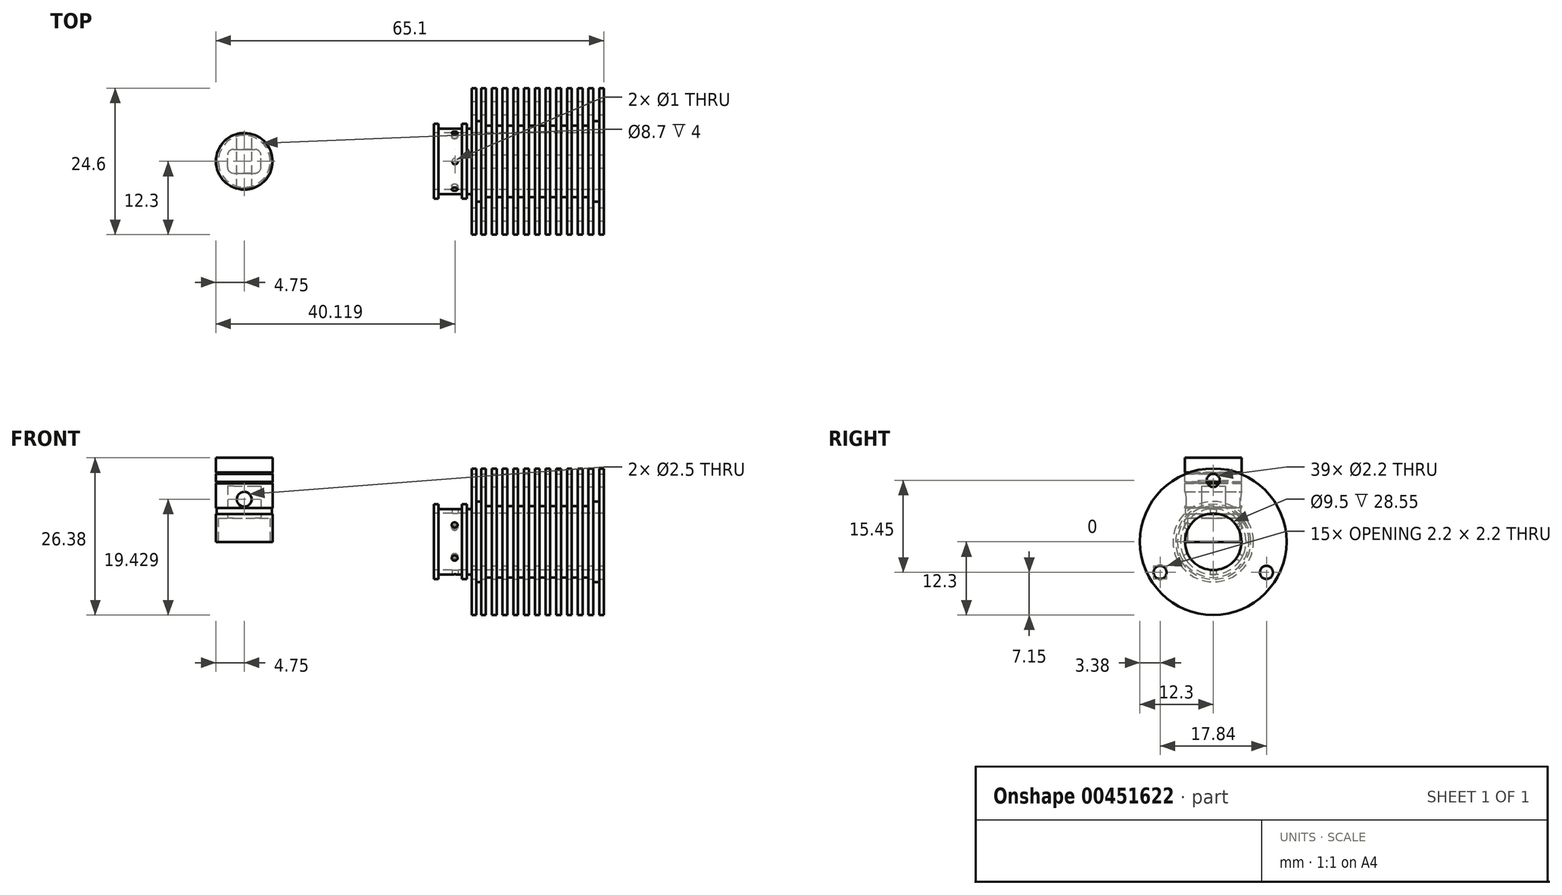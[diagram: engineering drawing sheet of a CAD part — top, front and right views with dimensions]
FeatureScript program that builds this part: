
annotation { "Feature Type Name" : "Feature", "Feature Type Description" : "" }
export const myFeature = defineFeature(function(context is Context, id is Id, definition is map)
    precondition{}
    {
        {
            var Q0;
            Q0=qCreatedBy(makeId("Front.planeOp"),FACE);
            var sketch = newSketch(context, id + "F0", { "sketchPlane" : qUnion([Q0])});
            skPoint(sketch, "E0.middle", {"position": v(0, 0) * mm});
            skLineSegment(sketch, "E1", {"start": v(0, -0.02) * mm, "end": v(0, 14.08) * mm});
            skLineSegment(sketch, "E2", {"start": v(-4.75, 14.08) * mm, "end": v(-4.75, 11.63) * mm});
            skLineSegment(sketch, "E3", {"start": v(-4.75, 4.68) * mm, "end": v(-4.62, 4.68) * mm});
            skLineSegment(sketch, "E4", {"start": v(-4.62, 4.68) * mm, "end": v(-4.62, 5.68) * mm});
            skLineSegment(sketch, "E5", {"start": v(-4.62, 5.68) * mm, "end": v(-4.75, 5.68) * mm});
            skLineSegment(sketch, "E6", {"start": v(-4.75, 10.03) * mm, "end": v(-4.62, 9.9) * mm});
            skLineSegment(sketch, "E7", {"start": v(-4.62, 9.9) * mm, "end": v(-4.75, 9.77) * mm});
            skLineSegment(sketch, "E8", {"start": v(-4.75, 11.63) * mm, "end": v(-4.62, 11.5) * mm});
            skLineSegment(sketch, "E9", {"start": v(-4.62, 11.5) * mm, "end": v(-4.75, 11.37) * mm});
            skLineSegment(sketch, "E10.trimOffspring", {"start": v(-4.75, 11.37) * mm, "end": v(-4.75, 10.03) * mm});
            skLineSegment(sketch, "E11.trimOffspring", {"start": v(-4.75, 9.77) * mm, "end": v(-4.75, 5.68) * mm});
            skLineSegment(sketch, "E12.trimOffspring", {"start": v(-4.75, 4.68) * mm, "end": v(-4.75, -0.02) * mm});
            skLineSegment(sketch, "E13", {"start": v(-4.75, 14.08) * mm, "end": v(0, 14.08) * mm});
            skLineSegment(sketch, "E14", {"start": v(-4.75, -0.02) * mm, "end": v(0, -0.02) * mm});
            skLineSegment(sketch, "E15", {"start": v(0, 14.08) * mm, "end": v(0, -6.41) * mm, "construction": true});
            skSolve(sketch);
        }
        {
            var Q0;
            {var subQ0=sQuery(id+"F0.wireOp",EDGE,"eGdi0r23-MWlI-d9Id-6IcZ-tQ7A4gUvsILz.left");Q0=makeQuery(id+"F0.imprint","IMPRINT",FACE,{"disambiguationData":[TD([[makeQuery(id+"F0.imprint","IMPRINT",EDGE,{"derivedFrom":subQ0}),1.0]])]});}
            var Q1;
            Q1=makeQuery(id+"F0.imprint","IMPRINT",FACE,{"disambiguationData":[TD([[makeQuery(id+"F0.imprint","IMPRINT",EDGE,{"derivedFrom":sQuery(id+"F0.wireOp",EDGE,"E1")}),1.0]])]});
            var Q2;
            Q2=sQuery(id+"F0.wireOp",EDGE,"E15");
            revolve(context, id + "F1", {"entities" : qUnion([Q0, Q1]), "axis" : qUnion([Q2]), "revolveType" : RevolveType.FULL});
        }
        {
            var Q0;
            Q0=qCreatedBy(makeId("Front.planeOp"),FACE);
            var sketch = newSketch(context, id + "F2", { "sketchPlane" : qUnion([Q0])});
            skPoint(sketch, "E16", {"position": v(0, 7.13) * mm});
            skCircle(sketch, "E17", {"center": v(0, 7.13) * mm, "radius": 1.25 * mm});
            skSolve(sketch);
        }
        {
            var Q0;
            Q0=makeQuery(id+"F2.imprint","IMPRINT",FACE,{"disambiguationData":[TD([[makeQuery(id+"F2.imprint","IMPRINT",EDGE,{"derivedFrom":sQuery(id+"F2.wireOp",EDGE,"E17")}),1.0]])]});
            extrude(context, id + "F3", {"entities" : qUnion([Q0]), "operationType" : NewBodyOperationType.REMOVE, "endBound" : BoundingType.SYMMETRIC, "depth" : 10 * mm});
        }
        {
            var Q0;
            Q0=makeQuery(id+"F1.opRevolve","SWEPT_FACE",FACE,{"disambiguationData":[OSD([sQuery(id+"F0.wireOp",EDGE,"E14")])]});
            var sketch = newSketch(context, id + "F4", { "sketchPlane" : qUnion([Q0])});
            skLineSegment(sketch, "E18.bottom", {"start": v(-1.8, 2) * mm, "end": v(1.8, 2) * mm});
            skLineSegment(sketch, "E18.top", {"start": v(-1.8, -2) * mm, "end": v(1.8, -2) * mm});
            skLineSegment(sketch, "E18.left", {"start": v(-2.8, 1) * mm, "end": v(-2.8, -1) * mm});
            skLineSegment(sketch, "E18.right", {"start": v(2.8, 1) * mm, "end": v(2.8, -1) * mm});
            skPoint(sketch, "E18.middle", {"position": v(0, 0) * mm});
            skCircle(sketch, "E19", {"center": v(0, 0) * mm, "radius": 4.35 * mm});
            skPoint(sketch, "E20.visualSharp", {"position": v(-2.8, 2) * mm});
            skArc(sketch, "E20.filletArc", {"start": v(-1.8, 2) * mm, "mid": v(-2.5, 1.7) * mm, "end": v(-2.8, 1) * mm});
            skPoint(sketch, "E21.visualSharp", {"position": v(-2.8, -2) * mm});
            skArc(sketch, "E21.filletArc", {"start": v(-2.8, -1) * mm, "mid": v(-2.5, -1.7) * mm, "end": v(-1.8, -2) * mm});
            skPoint(sketch, "E22.visualSharp", {"position": v(2.8, 2) * mm});
            skArc(sketch, "E22.filletArc", {"start": v(2.8, 1) * mm, "mid": v(2.5, 1.7) * mm, "end": v(1.8, 2) * mm});
            skPoint(sketch, "E23.visualSharp", {"position": v(2.8, -2) * mm});
            skArc(sketch, "E23.filletArc", {"start": v(1.8, -2) * mm, "mid": v(2.5, -1.7) * mm, "end": v(2.8, -1) * mm});
            skSolve(sketch);
        }
        {
            var Q0;
            Q0=makeQuery(id+"F4.imprint","IMPRINT",FACE,{"disambiguationData":[TD([[makeQuery(id+"F4.imprint","IMPRINT",EDGE,{"derivedFrom":sQuery(id+"F4.wireOp",EDGE,"E18.bottom")}),1.0]])]});
            var Q1;
            Q1=sQuery(id+"FsbAGgwMZmhRhTR_1.wireOp",EDGE,"XXkkC4YT-YGF8-Mw8t-M4hJ-ITye5uaQiXAc");
            extrude(context, id + "F5", {"entities" : qUnion([Q0]), "operationType" : NewBodyOperationType.REMOVE, "surfaceEntities" : qUnion([Q1]), "oppositeDirection" : true, "depth" : 4 * mm});
        }
        {
            var Q0;
            Q0=makeQuery(id+"F5.boolean.opBoolean","SPLIT",FACE,{"disambiguationData":[TD([makeQuery(id+"F5.opExtrude","SWEPT_FACE",FACE,{"disambiguationData":[OSD([sQuery(id+"F4.wireOp",EDGE,"E18.bottom")])]})])],"derivedFrom":makeQuery(id+"F1.opRevolve","SWEPT_FACE",FACE,{"disambiguationData":[OSD([sQuery(id+"F0.wireOp",EDGE,"E14")])]})});
            extrude(context, id + "F6", {"entities" : qUnion([Q0]), "operationType" : NewBodyOperationType.REMOVE, "oppositeDirection" : true, "depth" : 9.4 * mm});
        }
        {
            var Q0;
            Q0=qCreatedBy(makeId("Front.planeOp"),FACE);
            var sketch = newSketch(context, id + "F7", { "sketchPlane" : qUnion([Q0])});
            skPoint(sketch, "E24.0", {"position": v(0, 7.13) * mm});
            skCircle(sketch, "E24.1", {"center": v(0, 7.13) * mm, "radius": 1.25 * mm});
            skSolve(sketch);
        }
        {
            var Q0;
            Q0=makeQuery(id+"F7.imprint","IMPRINT",FACE,{"disambiguationData":[TD([[makeQuery(id+"F7.imprint","IMPRINT",EDGE,{"derivedFrom":sQuery(id+"F7.wireOp",EDGE,"E24.1")}),1.0]])]});
            extrude(context, id + "F8", {"entities" : qUnion([Q0]), "endBound" : BoundingType.SYMMETRIC, "depth" : 9 * mm});
        }
        {
            var Q0;
            Q0=qCreatedBy(makeId("Front.planeOp"),FACE);
            var sketch = newSketch(context, id + "F9", { "sketchPlane" : qUnion([Q0])});
            skLineSegment(sketch, "E25", {"start": v(27.89, 0) * mm, "end": v(63.64, 0) * mm, "construction": true});
            skLineSegment(sketch, "E26", {"start": v(31.8, 4.75) * mm, "end": v(60.35, 4.75) * mm});
            skLineSegment(sketch, "E27", {"start": v(60.35, 4.75) * mm, "end": v(60.35, 12.3) * mm});
            skLineSegment(sketch, "E28", {"start": v(59.55, 12.3) * mm, "end": v(59.55, 6.75) * mm});
            skLineSegment(sketch, "E29", {"start": v(59.55, 6.75) * mm, "end": v(58.55, 6.75) * mm});
            skLineSegment(sketch, "E30", {"start": v(60.35, 12.3) * mm, "end": v(59.55, 12.3) * mm});
            skLineSegment(sketch, "E31", {"start": v(40.24, 12.3) * mm, "end": v(39.75, 12.3) * mm});
            skLineSegment(sketch, "E32", {"start": v(39.75, 12.3) * mm, "end": v(39.75, 6.75) * mm});
            skLineSegment(sketch, "E33", {"start": v(38.95, 12.3) * mm, "end": v(38.15, 12.3) * mm});
            skLineSegment(sketch, "E34", {"start": v(38.15, 12.3) * mm, "end": v(38.15, 5.8) * mm});
            skLineSegment(sketch, "E35", {"start": v(38.95, 12.3) * mm, "end": v(38.95, 6.75) * mm});
            skLineSegment(sketch, "E36", {"start": v(38.95, 6.75) * mm, "end": v(39.75, 6.75) * mm});
            skLineSegment(sketch, "E37", {"start": v(31.8, 4.75) * mm, "end": v(31.8, 6.3) * mm});
            skLineSegment(sketch, "E38", {"start": v(31.8, 6.3) * mm, "end": v(32.6, 6.3) * mm});
            skLineSegment(sketch, "E39", {"start": v(32.6, 6.3) * mm, "end": v(32.6, 5.8) * mm});
            skLineSegment(sketch, "E40", {"start": v(32.9, 5.5) * mm, "end": v(36.25, 5.5) * mm});
            skLineSegment(sketch, "E41", {"start": v(36.55, 5.8) * mm, "end": v(36.55, 6.3) * mm});
            skLineSegment(sketch, "E42", {"start": v(36.55, 6.3) * mm, "end": v(37.35, 6.3) * mm});
            skLineSegment(sketch, "E43", {"start": v(37.35, 6.3) * mm, "end": v(37.35, 5.8) * mm});
            skLineSegment(sketch, "E44", {"start": v(37.65, 5.5) * mm, "end": v(37.85, 5.5) * mm});
            skLineSegment(sketch, "E45", {"start": v(58.55, 6.75) * mm, "end": v(58.55, 12.3) * mm});
            skLineSegment(sketch, "E46", {"start": v(58.55, 12.3) * mm, "end": v(57.75, 12.3) * mm});
            skLineSegment(sketch, "E47", {"start": v(57.75, 12.3) * mm, "end": v(57.75, 6) * mm});
            skLineSegment(sketch, "E48", {"start": v(57.75, 6) * mm, "end": v(56.75, 6) * mm});
            skLineSegment(sketch, "E49", {"start": v(56.75, 6) * mm, "end": v(56.75, 12.3) * mm});
            skLineSegment(sketch, "E50", {"start": v(56.75, 12.3) * mm, "end": v(55.95, 12.3) * mm});
            skLineSegment(sketch, "E51", {"start": v(55.95, 12.3) * mm, "end": v(55.95, 6) * mm});
            skLineSegment(sketch, "E52.1.0.0", {"start": v(55.95, 6) * mm, "end": v(54.95, 6) * mm});
            skLineSegment(sketch, "E52.1.0.1", {"start": v(54.95, 6) * mm, "end": v(54.95, 12.3) * mm});
            skLineSegment(sketch, "E52.1.0.2", {"start": v(54.95, 12.3) * mm, "end": v(54.15, 12.3) * mm});
            skLineSegment(sketch, "E52.1.0.3", {"start": v(54.15, 12.3) * mm, "end": v(54.15, 6) * mm});
            skLineSegment(sketch, "E52.2.0.0", {"start": v(54.15, 6) * mm, "end": v(53.15, 6) * mm});
            skLineSegment(sketch, "E52.2.0.1", {"start": v(53.15, 6) * mm, "end": v(53.15, 12.3) * mm});
            skLineSegment(sketch, "E52.2.0.2", {"start": v(53.15, 12.3) * mm, "end": v(52.35, 12.3) * mm});
            skLineSegment(sketch, "E52.2.0.3", {"start": v(52.35, 12.3) * mm, "end": v(52.35, 6) * mm});
            skLineSegment(sketch, "E52.3.0.0", {"start": v(52.35, 6) * mm, "end": v(51.35, 6) * mm});
            skLineSegment(sketch, "E52.3.0.1", {"start": v(51.35, 6) * mm, "end": v(51.35, 12.3) * mm});
            skLineSegment(sketch, "E52.3.0.2", {"start": v(51.35, 12.3) * mm, "end": v(50.55, 12.3) * mm});
            skLineSegment(sketch, "E52.3.0.3", {"start": v(50.55, 12.3) * mm, "end": v(50.55, 6) * mm});
            skLineSegment(sketch, "E52.4.0.0", {"start": v(50.55, 6) * mm, "end": v(49.55, 6) * mm});
            skLineSegment(sketch, "E52.4.0.1", {"start": v(49.55, 6) * mm, "end": v(49.55, 12.3) * mm});
            skLineSegment(sketch, "E52.4.0.2", {"start": v(49.55, 12.3) * mm, "end": v(48.75, 12.3) * mm});
            skLineSegment(sketch, "E52.4.0.3", {"start": v(48.75, 12.3) * mm, "end": v(48.75, 6) * mm});
            skLineSegment(sketch, "E52.5.0.0", {"start": v(48.75, 6) * mm, "end": v(47.75, 6) * mm});
            skLineSegment(sketch, "E52.5.0.1", {"start": v(47.75, 6) * mm, "end": v(47.75, 12.3) * mm});
            skLineSegment(sketch, "E52.5.0.2", {"start": v(47.75, 12.3) * mm, "end": v(46.95, 12.3) * mm});
            skLineSegment(sketch, "E52.5.0.3", {"start": v(46.95, 12.3) * mm, "end": v(46.95, 6) * mm});
            skLineSegment(sketch, "E52.6.0.0", {"start": v(46.95, 6) * mm, "end": v(45.95, 6) * mm});
            skLineSegment(sketch, "E52.6.0.1", {"start": v(45.95, 6) * mm, "end": v(45.95, 12.3) * mm});
            skLineSegment(sketch, "E52.6.0.2", {"start": v(45.95, 12.3) * mm, "end": v(45.15, 12.3) * mm});
            skLineSegment(sketch, "E52.6.0.3", {"start": v(45.15, 12.3) * mm, "end": v(45.15, 6) * mm});
            skLineSegment(sketch, "E52.7.0.0", {"start": v(45.15, 6) * mm, "end": v(44.15, 6) * mm});
            skLineSegment(sketch, "E52.7.0.1", {"start": v(44.15, 6) * mm, "end": v(44.15, 12.3) * mm});
            skLineSegment(sketch, "E52.7.0.2", {"start": v(44.15, 12.3) * mm, "end": v(43.35, 12.3) * mm});
            skLineSegment(sketch, "E52.7.0.3", {"start": v(43.35, 12.3) * mm, "end": v(43.35, 6) * mm});
            skLineSegment(sketch, "E52.8.0.0", {"start": v(43.35, 6) * mm, "end": v(42.35, 6) * mm});
            skLineSegment(sketch, "E52.8.0.1", {"start": v(42.35, 6) * mm, "end": v(42.35, 12.3) * mm});
            skLineSegment(sketch, "E52.8.0.2", {"start": v(42.35, 12.3) * mm, "end": v(41.55, 12.3) * mm});
            skLineSegment(sketch, "E52.8.0.3", {"start": v(41.55, 12.3) * mm, "end": v(41.55, 6) * mm});
            skLineSegment(sketch, "E52.9.0.0", {"start": v(41.55, 6) * mm, "end": v(40.55, 6) * mm});
            skLineSegment(sketch, "E52.9.0.1", {"start": v(40.55, 6) * mm, "end": v(40.55, 12.3) * mm});
            skLineSegment(sketch, "E52.9.0.2", {"start": v(40.55, 12.3) * mm, "end": v(39.75, 12.3) * mm});
            skLineSegment(sketch, "E52.9.0.3", {"start": v(39.75, 12.3) * mm, "end": v(39.75, 6) * mm});
            skLineSegment(sketch, "E52.direction1", {"start": v(56.75, 6) * mm, "end": v(54.95, 6) * mm, "construction": true});
            skPoint(sketch, "E53.visualSharp", {"position": v(37.35, 5.5) * mm});
            skArc(sketch, "E53.filletArc", {"start": v(37.35, 5.8) * mm, "mid": v(37.44, 5.59) * mm, "end": v(37.65, 5.5) * mm});
            skPoint(sketch, "E54.visualSharp", {"position": v(32.6, 5.5) * mm});
            skArc(sketch, "E54.filletArc", {"start": v(32.6, 5.8) * mm, "mid": v(32.69, 5.59) * mm, "end": v(32.9, 5.5) * mm});
            skPoint(sketch, "E55.visualSharp", {"position": v(38.15, 5.5) * mm});
            skArc(sketch, "E55.filletArc", {"start": v(37.85, 5.5) * mm, "mid": v(38.06, 5.59) * mm, "end": v(38.15, 5.8) * mm});
            skPoint(sketch, "E56.visualSharp", {"position": v(36.55, 5.5) * mm});
            skArc(sketch, "E56.filletArc", {"start": v(36.25, 5.5) * mm, "mid": v(36.46, 5.59) * mm, "end": v(36.55, 5.8) * mm});
            skPoint(sketch, "E57", {"position": v(35.3, 5.5) * mm});
            skSolve(sketch);
        }
        {
            var Q0;
            {var subQ0=sQuery(id+"F9.wireOp",EDGE,"E27");Q0=makeQuery(id+"F9.imprint","IMPRINT",FACE,{"disambiguationData":[TD([[makeQuery(id+"F9.imprint","IMPRINT",EDGE,{"derivedFrom":subQ0}),1.0]])]});}
            var Q1;
            Q1=sQuery(id+"F9.wireOp",EDGE,"E25");
            revolve(context, id + "F10", {"entities" : qUnion([Q0]), "axis" : qUnion([Q1]), "revolveType" : RevolveType.FULL});
        }
        {
            var Q0;
            Q0=makeQuery(id+"F10.opRevolve","SWEPT_FACE",FACE,{"disambiguationData":[OSD([sQuery(id+"F9.wireOp",EDGE,"E27")])]});
            var sketch = newSketch(context, id + "F11", { "sketchPlane" : qUnion([Q0])});
            skCircle(sketch, "E58", {"center": v(0, 0) * mm, "radius": 10.3 * mm, "construction": true});
            skPoint(sketch, "E59", {"position": v(0, 10.3) * mm});
            skPoint(sketch, "E60.1.1", {"position": v(-8.92, -5.15) * mm});
            skPoint(sketch, "E60.2.1", {"position": v(8.92, -5.15) * mm});
            skSolve(sketch);
        }
        {
            var Q0;
            Q0=sQuery(id+"F11.wireOp",VERTEX,"E59");
            var Q1;
            Q1=sQuery(id+"F11.wireOp",VERTEX,"E60.1.1");
            var Q2;
            Q2=sQuery(id+"F11.wireOp",VERTEX,"E60.2.1");
            var Q3;
            Q3=makeQuery(id+"F10.opRevolve","SWEPT_BODY",BODY,{"disambiguationData":[OSD([sQuery(id+"F9.wireOp",EDGE,"E26"),sQuery(id+"F9.wireOp",EDGE,"E27"),sQuery(id+"F9.wireOp",EDGE,"E28"),sQuery(id+"F9.wireOp",EDGE,"E29"),sQuery(id+"F9.wireOp",EDGE,"E30"),sQuery(id+"F9.wireOp",EDGE,"E33"),sQuery(id+"F9.wireOp",EDGE,"E34"),sQuery(id+"F9.wireOp",EDGE,"E35"),sQuery(id+"F9.wireOp",EDGE,"E36"),sQuery(id+"F9.wireOp",EDGE,"E37"),sQuery(id+"F9.wireOp",EDGE,"E38"),sQuery(id+"F9.wireOp",EDGE,"E39"),sQuery(id+"F9.wireOp",EDGE,"E40"),sQuery(id+"F9.wireOp",EDGE,"E41"),sQuery(id+"F9.wireOp",EDGE,"E42"),sQuery(id+"F9.wireOp",EDGE,"E43"),sQuery(id+"F9.wireOp",EDGE,"E44"),sQuery(id+"F9.wireOp",EDGE,"E45"),sQuery(id+"F9.wireOp",EDGE,"E46"),sQuery(id+"F9.wireOp",EDGE,"E47"),sQuery(id+"F9.wireOp",EDGE,"E48"),sQuery(id+"F9.wireOp",EDGE,"E49"),sQuery(id+"F9.wireOp",EDGE,"E50"),sQuery(id+"F9.wireOp",EDGE,"E51"),sQuery(id+"F9.wireOp",EDGE,"E52.1.0.0"),sQuery(id+"F9.wireOp",EDGE,"E52.1.0.1"),sQuery(id+"F9.wireOp",EDGE,"E52.1.0.2"),sQuery(id+"F9.wireOp",EDGE,"E52.1.0.3"),sQuery(id+"F9.wireOp",EDGE,"E52.2.0.0"),sQuery(id+"F9.wireOp",EDGE,"E52.2.0.1"),sQuery(id+"F9.wireOp",EDGE,"E52.2.0.2"),sQuery(id+"F9.wireOp",EDGE,"E52.2.0.3"),sQuery(id+"F9.wireOp",EDGE,"E52.3.0.0"),sQuery(id+"F9.wireOp",EDGE,"E52.3.0.1"),sQuery(id+"F9.wireOp",EDGE,"E52.3.0.2"),sQuery(id+"F9.wireOp",EDGE,"E52.3.0.3"),sQuery(id+"F9.wireOp",EDGE,"E52.4.0.0"),sQuery(id+"F9.wireOp",EDGE,"E52.4.0.1"),sQuery(id+"F9.wireOp",EDGE,"E52.4.0.2"),sQuery(id+"F9.wireOp",EDGE,"E52.4.0.3"),sQuery(id+"F9.wireOp",EDGE,"E52.5.0.0"),sQuery(id+"F9.wireOp",EDGE,"E52.5.0.1"),sQuery(id+"F9.wireOp",EDGE,"E52.5.0.2"),sQuery(id+"F9.wireOp",EDGE,"E52.5.0.3"),sQuery(id+"F9.wireOp",EDGE,"E52.6.0.0"),sQuery(id+"F9.wireOp",EDGE,"E52.6.0.1"),sQuery(id+"F9.wireOp",EDGE,"E52.6.0.2"),sQuery(id+"F9.wireOp",EDGE,"E52.6.0.3"),sQuery(id+"F9.wireOp",EDGE,"E52.7.0.0"),sQuery(id+"F9.wireOp",EDGE,"E52.7.0.1"),sQuery(id+"F9.wireOp",EDGE,"E52.7.0.2"),sQuery(id+"F9.wireOp",EDGE,"E52.7.0.3"),sQuery(id+"F9.wireOp",EDGE,"E52.8.0.0"),sQuery(id+"F9.wireOp",EDGE,"E52.8.0.1"),sQuery(id+"F9.wireOp",EDGE,"E52.8.0.2"),sQuery(id+"F9.wireOp",EDGE,"E52.8.0.3"),sQuery(id+"F9.wireOp",EDGE,"E52.9.0.0"),sQuery(id+"F9.wireOp",EDGE,"E52.9.0.1"),sQuery(id+"F9.wireOp",EDGE,"E52.9.0.2"),sQuery(id+"F9.wireOp",EDGE,"E52.9.0.3"),sQuery(id+"F9.wireOp",EDGE,"E53.filletArc"),sQuery(id+"F9.wireOp",EDGE,"E54.filletArc"),sQuery(id+"F9.wireOp",EDGE,"E55.filletArc"),sQuery(id+"F9.wireOp",EDGE,"E56.filletArc")])]});
            hole(context, id + "F12", {"style" : HoleStyle.SIMPLE, "endStyle" : HoleEndStyle.THROUGH, "holeDiameter" : 2.2 * mm, "startFromSketch" : true, "locations" : qUnion([Q0, Q1, Q2]), "scope" : qUnion([Q3]), "isTappedThrough" : true});
        }
        {
            var Q0;
            Q0=qCreatedBy(makeId("Top.planeOp"),FACE);
            var sketch = newSketch(context, id + "F13", { "sketchPlane" : qUnion([Q0])});
            skCircle(sketch, "E61", {"center": v(35.37, 0) * mm, "radius": 0.5 * mm});
            skSolve(sketch);
        }
        {
            var Q0;
            Q0=qSketchRegion(id+"F13",true);
            var Q1;
            Q1=sQuery(id+"F13.wireOp",EDGE,"E61");
            extrude(context, id + "F14", {"entities" : qUnion([Q0]), "operationType" : NewBodyOperationType.REMOVE, "surfaceEntities" : qUnion([Q1]), "endBound" : BoundingType.SYMMETRIC, "depth" : 13 * mm});
        }
        {
            var Q0;
            Q0=qCreatedBy(makeId("Front.planeOp"),FACE);
            var Q1;
            Q1=sQuery(id+"F9.wireOp",EDGE,"E25");
            cPlane(context, id + "F15", {"entities" : qUnion([Q0, Q1]), "cplaneType" : CPlaneType.LINE_ANGLE, "offset" : 150 * mm, "angle" : 30 * degree, "width" : 150 * mm, "height" : 150 * mm});
        }
        {
            var Q0;
            Q0=qCreatedBy(id+"F15.planeOp",FACE);
            var sketch = newSketch(context, id + "F16", { "sketchPlane" : qUnion([Q0])});
            skPoint(sketch, "E62", {"position": v(-35.3, 0) * mm});
            skCircle(sketch, "E63", {"center": v(-35.3, 0) * mm, "radius": 0.5 * mm});
            skSolve(sketch);
        }
        {
            var Q0;
            Q0=qSketchRegion(id+"F16",true);
            var Q1;
            Q1=sQuery(id+"F16.wireOp",EDGE,"E63");
            extrude(context, id + "F17", {"entities" : qUnion([Q0]), "operationType" : NewBodyOperationType.REMOVE, "surfaceEntities" : qUnion([Q1]), "endBound" : BoundingType.SYMMETRIC, "depth" : 13 * mm});
        }
        {
            var Q0;
            Q0=qCreatedBy(makeId("Top.planeOp"),FACE);
            var Q1;
            Q1=sQuery(id+"F9.wireOp",EDGE,"E25");
            cPlane(context, id + "F18", {"entities" : qUnion([Q0, Q1]), "cplaneType" : CPlaneType.LINE_ANGLE, "offset" : 150 * mm, "angle" : 59 * degree, "width" : 150 * mm, "height" : 150 * mm});
        }
        {
            var Q0;
            Q0=qCreatedBy(id+"F18.planeOp",FACE);
            var sketch = newSketch(context, id + "F19", { "sketchPlane" : qUnion([Q0])});
            skPoint(sketch, "E64", {"position": v(-35.3, 0) * mm});
            skCircle(sketch, "E65", {"center": v(-35.3, 0) * mm, "radius": 0.5 * mm});
            skSolve(sketch);
        }
        {
            var Q0;
            Q0=qSketchRegion(id+"F19",true);
            var Q1;
            Q1=sQuery(id+"F19.wireOp",EDGE,"E65");
            extrude(context, id + "F20", {"entities" : qUnion([Q0]), "operationType" : NewBodyOperationType.REMOVE, "surfaceEntities" : qUnion([Q1]), "endBound" : BoundingType.SYMMETRIC, "depth" : 13 * mm});
        }
    });
